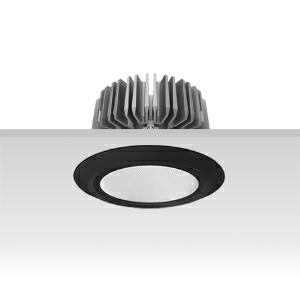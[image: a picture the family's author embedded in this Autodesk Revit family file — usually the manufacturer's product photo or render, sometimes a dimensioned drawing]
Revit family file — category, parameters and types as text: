
# Revit family: 3f_filippi_-_3f_reno_bianco_ampio_3f_filippi_-_30375_a01036_-_3f_reno_150_wh_2000-840_dali_wide___vs_bk_336f
name_source: partatom
category: Lighting Fixtures
units: mm (PartAtom-declared; Revit-internal decimal feet)

## family parameters
Cut with Voids When Loaded = No
Host = Face
Light Source = No
Part Type = Normal
Room Calculation Point = No
Round Connector Dimension = Use Diameter
Shared = No

## types (1)
- 3F Filippi - 3F Reno Bianco Ampio (1 x LED, 1709 lm, 20 W, 4000 K)
    Apparent Load = 20 VA
    Approval mark = CE
    CIE Flux Codes = 74 93 99 100 100
    Color Rendering = 80
    Color Temperature = 4000 K
    Control Gear = Electronic transformer
    Default Elevation = 1800 mm
    Description = ILLUMINOTECHNICAL
Luminous efficiency 100% (DLOR 100%, ULOR 0%).
Initial luminous flux of the luminaire 1709 lm.
Direct symmetric wide distribution.
Installation Interdistance Transv.D = 1.12 x hu - Long.D = 1.11 x hu.
Tabular UGR (CIE 117 - 4H-8H; S=0.25H; 70/50/20): RUG 22.8 - 22.7.
Beam angle: 74° - 73°.
Luminous efficacy 85 lm/W.
Lifetime (L90/B10): 30000 h. (tq+25°C)
Lifetime (L85/B10): 50000 h. (tq+25°C)
Lifetime (L70/B10): 80000 h. (tq+25°C)
Sudden decreased luminous flux after 50000 hours: 0% (C0).
Photobiological safety in compliance with IEC/TR 62778: RG0 risk exempt, (IEC 62471).
In compliance with IEC/EN 62722-2-1 - IEC/EN 62717 standards.

SOURCE
Compact LED module 2000/840.
Energy efficiency class (UE 2019/2020 - UE 2019/2015): D.
CIE 13.3 Colour rendering index: CRI >80 (R9 <50%).
IES TM-30 Fidelity Index: Rf = 84 Rg = 95.
CCT nominal colour temperature 4000 K.
Colour initial tolerance (MacAdam): SDCM 3.
Zhaga Book 3 compliant.

MECHANICAL
Passive heat dissipator in die-casting aluminium, oversized, for optimum thermal management of the LED module.
Parabolic element with graduated/concentric rings in white polycarbonate.
Transparent external lens with glossy and satin differentiated surfaces, with a cooling and anti-insect system in methacrylate (PMMA).
Fastening spring clips in stainless steel.
Dimensions: diameter 176 mm, height 111 mm. Weight 0.84 kg.
IP44 protection degree for exposed part, IP20 for recessed part.
Mechanical strength to impacts IK06 (1 joule).
Glow-wire test resistance 650°C.

ELECTRICAL
Wiring on a separate unit.
Halogen Free DALI-2 DATI (Parts 251, 252, 253), PUSH-DIM, electronic wiring 230V-50/60Hz, power factor 0.90 at full load, THD <25%, constant output current, SELV, class II, 1 driver, 1 DALI addresse.
Power of the luminaire 20 W.
ENEC - CE.
SAFE FLICKER: PstLM=<1 and SVM=<0.4 (IEC TR 61547-1 and IEC TR 63158), to ensure a more comfortable and safe light.
Luminaire compliant with EN 60598-2-22 for power supply from a centralised emergency system CPSS (Central Power Supply System), not incorporated in the luminaire - high risk areas excluded. The default power and flux are 100% in AC and 100% in DC.
Ambient temperature from 0°C to +25°C.
Temperature class T6 max 85°C.
Relative humidity UR: <85%.

INSTALLATION
Pull-up recessed fitting.
False ceiling carving: 150 mm.
All accessories dedicated to this product are available on the Catalog and on our website www.3F-Filippi.com.

ACCESSORIES
A01036 - Anti-glare microprismatic VS moulded glass, tempered, not flammable, locked and in line with the trim, in black polycarbonate.

APPLICATIONS
Environments: architectural, commercial, exhibition areas, transit areas, corridors, shops, display windows, service areas.
In false ceilings with narrow voids.

LIGHT MANAGEMENT
Recommended minimum setting: 10%.
The luminaire, equipped with (DALI-2 DATI) driver, can be controlled manually with 3F Easy Dim technology or automatically/manually with wired or wireless DALI/D2D control systems.
The D2D driver guarantees interoperability with other devices with the same certification by making the following information available:
Device Data (Part 251), Energy Report (Part 252), Diagnosis & Maintenance (Part 253).
In electrical systems without a regulation system (manual or automatic) and DALI bus, a suitable jumper must be made on the DA-DA terminals of the appliance.

WARNING
Luminaire designed for disposal/recycling at end-of-life.
Replaceable (LED only) light source by a professional. Replaceable control gear by a professional.
    Height = 0 mm  [stored 0 ft]
    Lamp = 1 x LED
    Lamp Light Flux = 1709 lm
    Lamp Power = 20 W
    Lamp count = 1
    Length = 176 mm
    Lifetime = 50000 h
    Luminous efficacy = 85 lm/W
    Manufacturer = 3F Filippi
    ModVariant = No
    Model = 3F Filippi - 30375+A01036 - 3F Reno 150 WH 2000-840 DALI WIDE + VS BK
    Mounting Place = Ceiling
    Mounting Type = Recessed
    Number of Poles = 1
    OnlyDefault = Yes
    Power Factor = 1
    Product Name = 3F Filippi - 3F Reno Bianco Ampio
    Product group = recessed luminaire
    ProductGroupID = 4
    Protection Class = Protection class II
    Protection Degree = IP 20
    RLX_Detail_Level = 1
    RLX_Emergency_Light_Flux = 0 lm
    RLX_Emergency_Type = 0
    RLX_Emergency_Type_DB = No
    RlxData = <blob elided: 86997 chars, md5=5b16b809>
    Socket = socket
    Standby Power = 0 W
    System Light Flux = 1709 lm
    System Power = 20 W
    Type Comments = Product without accessories
    Type Image = 3ffilippi_3f_reno_150_bk_vs_smp.jpg
    URL = http://relux.com
    VarID = ---
    Voltage = 0 V
    Weight = 0.00 kg
    Width = 0 mm  [stored 0 ft]

note: [stored X ft] marks values corroborated as IEEE doubles in the binary element streams (Revit-internal decimal feet)

## geometry (parser evidence)
native form markers: Blend x4, Sweep x10
no freeform markers — native parametric forms only
